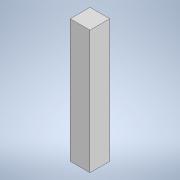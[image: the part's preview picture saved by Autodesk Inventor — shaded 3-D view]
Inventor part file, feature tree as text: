
AUTODESK INVENTOR PART (.ipt)
format: ipt  version: 2022 (Build 260153000, 153)  size: 92,672 bytes
history: native  units: mm
features: extrude x1, sketch x1
ambient origin geometry x8: Origin, YZ Plane, XZ Plane, XY Plane, X Axis, Y Axis, Z Axis, Center Point
bodies: Solid1 (feature_tree)
feature tree (2):
  extrude  "Extrusion1"  Depth=24.4mm
  sketch  "Sketch1"  dims[d0=24.4mm d1=24.4mm d2=152.4mm d3=0.0mm d4=0.5mm d5=0.872665mm]
